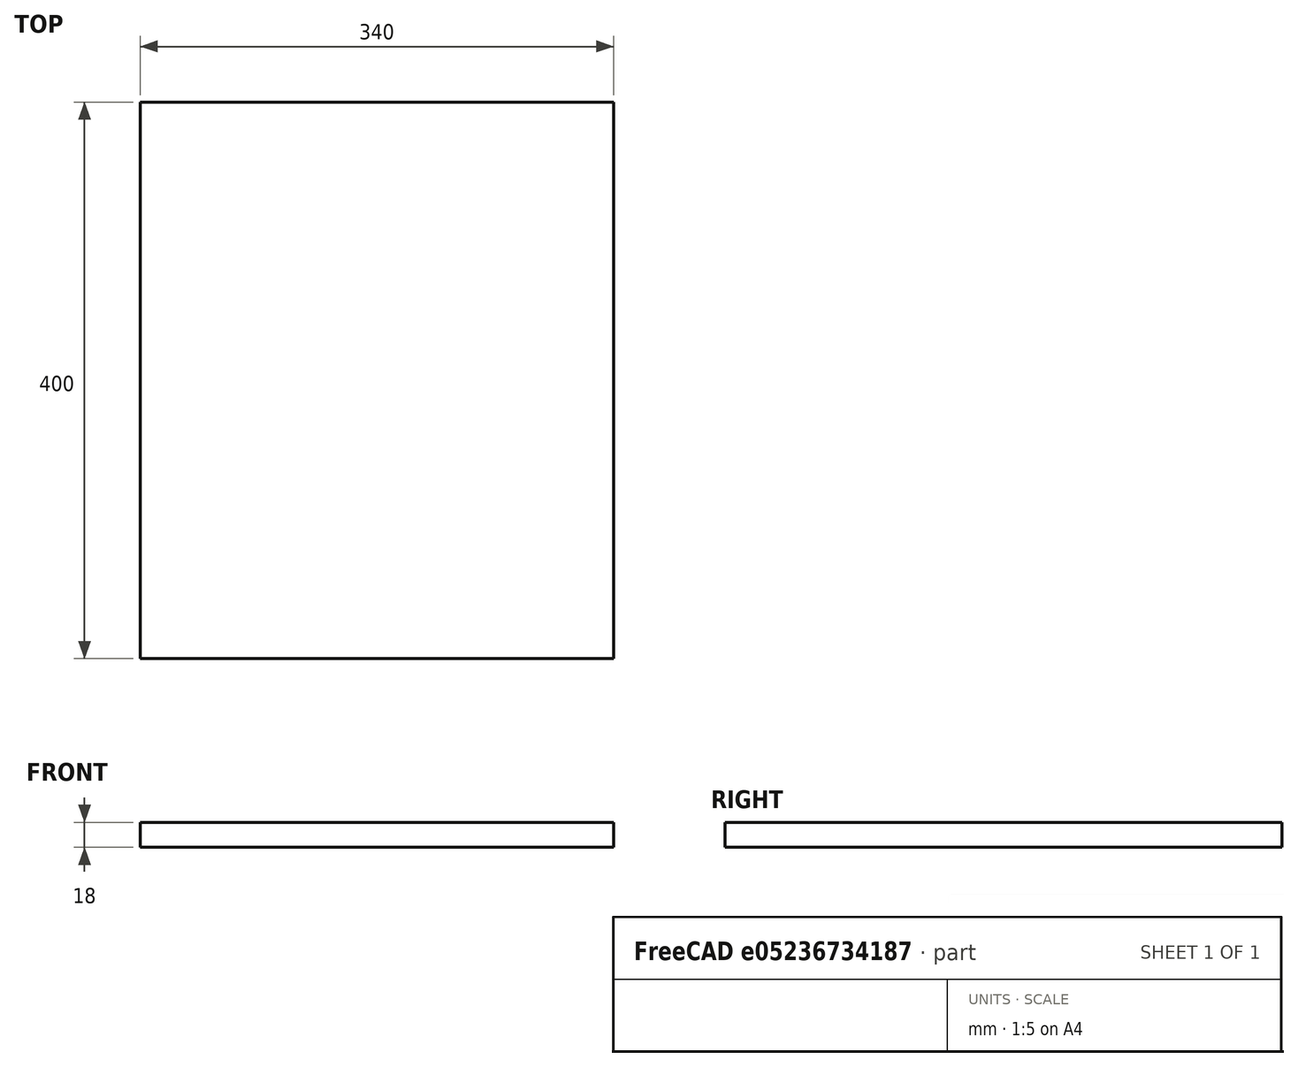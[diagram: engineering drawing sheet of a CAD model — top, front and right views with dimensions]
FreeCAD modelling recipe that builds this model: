
FCSTD DOCUMENT  (FreeCAD 0.18R4 (GitTag))
Label: vertical_shelf
License: All rights reserved
LicenseURL: http://en.wikipedia.org/wiki/All_rights_reserved
objects: Sketcher::SketchObject×1, PartDesign::Pad×1, PartDesign::Body×1
note: 4 computed .brp shape members not serialized (recipe doc carries the construction recipe); baked Part::Feature solids carry a one-line shape summary decoded from their .brp

FEATURE [Sketcher::SketchObject] Sketch
  MapMode = 5
  Support = -> [XY_Plane]
  sketch-geometry (4):
    g0: LineSegment StartX=0 StartY=0 StartZ=0 EndX=-340 EndY=0 EndZ=0
    g1: LineSegment StartX=-340 StartY=0 StartZ=0 EndX=-340 EndY=400 EndZ=0
    g2: LineSegment StartX=-340 StartY=400 StartZ=0 EndX=0 EndY=400 EndZ=0
    g3: LineSegment StartX=0 StartY=400 StartZ=0 EndX=0 EndY=0 EndZ=0
  constraints (11):
    c: Coincident(g0,g1)
    c: Coincident(g1,g2)
    c: Coincident(g2,g3)
    c: Coincident(g3,g0)
    c: Horizontal(g0)
    c: Horizontal(g2)
    c: Vertical(g1)
    c: Vertical(g3)
    c: Coincident(g0,g-1)
    c: DistanceY(g3,g3) = 400
    c: DistanceX(g0,g0) = 340
FEATURE [PartDesign::Pad] Pad001
  Length = 18
  Length2 = 100
  Profile = -> Sketch
  Type = 0
FEATURE [PartDesign::Body] Body
  Group = -> [Sketch,Pad001]
  Origin = -> Origin
  Tip = -> Pad001
